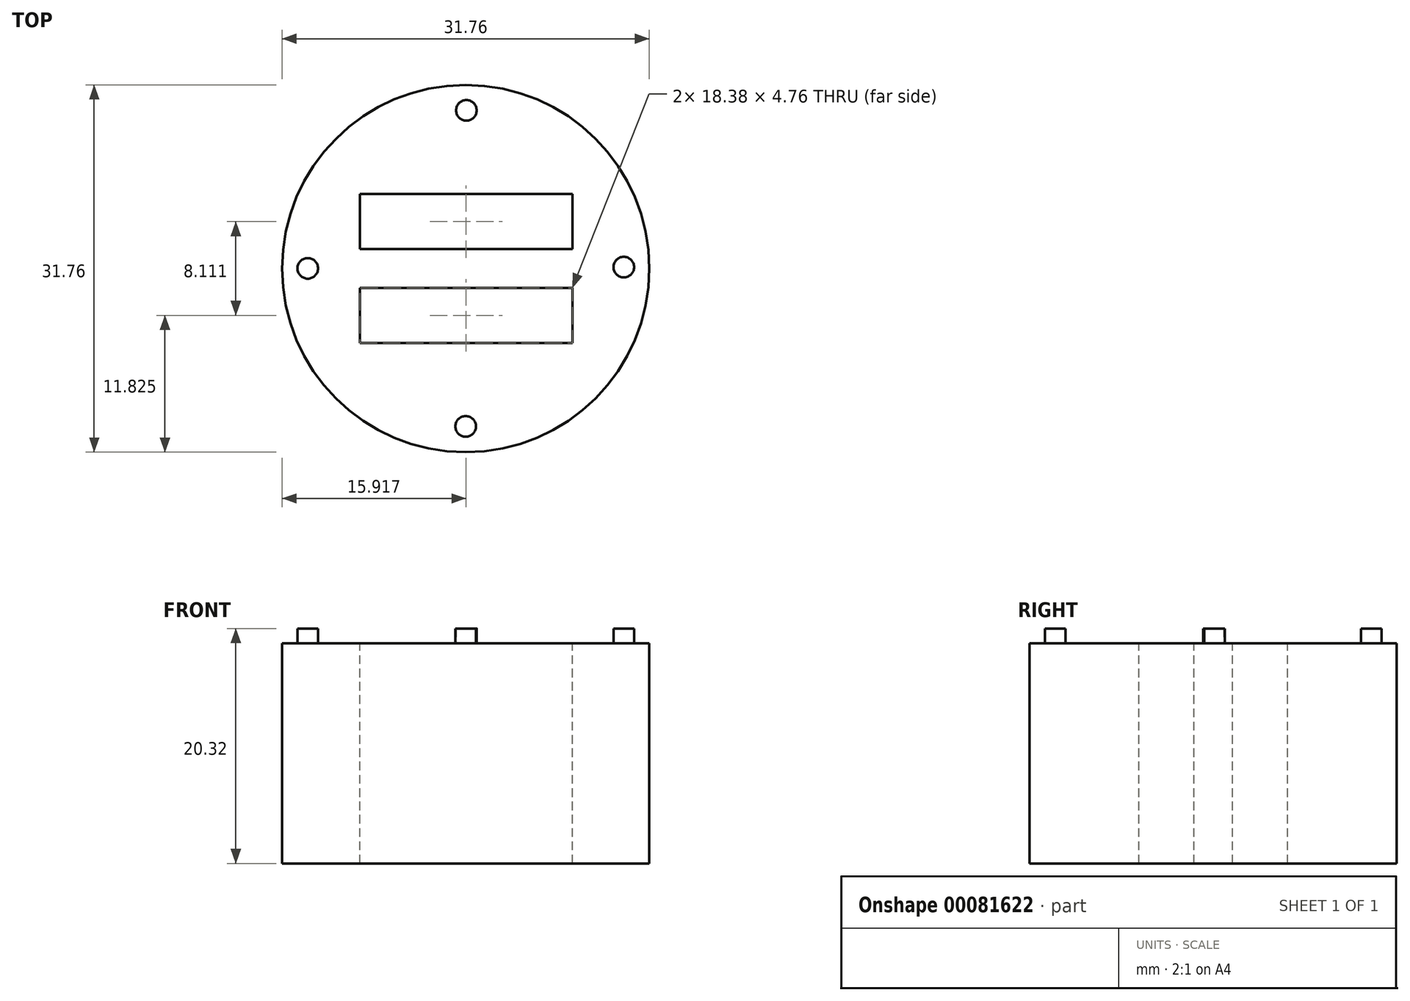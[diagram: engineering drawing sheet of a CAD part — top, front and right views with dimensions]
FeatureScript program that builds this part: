
annotation { "Feature Type Name" : "Feature", "Feature Type Description" : "" }
export const myFeature = defineFeature(function(context is Context, id is Id, definition is map)
    precondition{}
    {
        {
            var Q0;
            Q0=qCreatedBy(makeId("Top.planeOp"),FACE);
            var sketch = newSketch(context, id + "F0", { "sketchPlane" : qUnion([Q0])});
            skCircle(sketch, "E0", {"center": v(0, 0) * mm, "radius": 15.88 * mm});
            skSolve(sketch);
        }
        {
            var Q0;
            Q0=qSketchRegion(id+"F0",true);
            extrude(context, id + "F1", {"entities" : qUnion([Q0]), "depth" : 19.05 * mm});
        }
        {
            var Q0;
            Q0=makeQuery(id+"F1.opExtrude","CAP_FACE",FACE,{"disambiguationData":[OSD([sQuery(id+"F0.wireOp",EDGE,"E0")])],"isStart":true});
            var sketch = newSketch(context, id + "F2", { "sketchPlane" : qUnion([Q0])});
            skCircle(sketch, "E1", {"center": v(0, 0) * mm, "radius": 12.7 * mm});
            skSolve(sketch);
        }
        {
            var Q0;
            Q0=makeQuery(id+"F2.imprint","IMPRINT",FACE,{"disambiguationData":[TD([[makeQuery(id+"F2.imprint","IMPRINT",EDGE,{"derivedFrom":sQuery(id+"F2.wireOp",EDGE,"E1")}),-1.0]])]});
            var sketch = newSketch(context, id + "F3", { "sketchPlane" : qUnion([Q0])});
            skCircle(sketch, "E2", {"center": v(0, 13.65) * mm, "radius": 0.89 * mm});
            skCircle(sketch, "E3", {"center": v(-13.66, -0.02) * mm, "radius": 0.89 * mm});
            skCircle(sketch, "E4", {"center": v(0.06, -13.68) * mm, "radius": 0.89 * mm});
            skCircle(sketch, "E5", {"center": v(13.67, -0.12) * mm, "radius": 0.89 * mm});
            skSolve(sketch);
        }
        {
            var Q0;
            Q0=makeQuery(id+"F1.opExtrude","CAP_FACE",FACE,{"disambiguationData":[OSD([sQuery(id+"F0.wireOp",EDGE,"E0")])],"isStart":false});
            var sketch = newSketch(context, id + "F4", { "sketchPlane" : qUnion([Q0])});
            skLineSegment(sketch, "E6", {"start": v(0, 12.85) * mm, "end": v(0, -12.7) * mm});
            skLineSegment(sketch, "E7", {"start": v(0, -12.7) * mm, "end": v(-12.6, 0) * mm});
            skLineSegment(sketch, "E8", {"start": v(-12.6, 0) * mm, "end": v(0, 12.85) * mm});
            skLineSegment(sketch, "E9", {"start": v(0, 12.85) * mm, "end": v(12.68, 0) * mm});
            skLineSegment(sketch, "E10", {"start": v(12.68, 0) * mm, "end": v(0, -12.7) * mm});
            skLineSegment(sketch, "E11", {"start": v(-12.6, 0) * mm, "end": v(12.68, 0) * mm});
            skLineSegment(sketch, "E12", {"start": v(-6.3, -6.35) * mm, "end": v(9.08, 8.92) * mm});
            skLineSegment(sketch, "E13", {"start": v(-6.3, 6.43) * mm, "end": v(9.08, -9.08) * mm});
            skLineSegment(sketch, "E14", {"start": v(-6.3, -6.35) * mm, "end": v(-9.02, -9.05) * mm});
            skLineSegment(sketch, "E15", {"start": v(-6.3, 6.43) * mm, "end": v(-8.94, 9.08) * mm});
            skLineSegment(sketch, "E16", {"start": v(-8.94, 9.08) * mm, "end": v(-12.6, 0) * mm});
            skLineSegment(sketch, "E17", {"start": v(-12.6, 0) * mm, "end": v(-9.02, -9.05) * mm});
            skLineSegment(sketch, "E18", {"start": v(-9.02, -9.05) * mm, "end": v(0, -12.7) * mm});
            skLineSegment(sketch, "E19", {"start": v(0, -12.7) * mm, "end": v(9.08, -9.08) * mm});
            skLineSegment(sketch, "E20", {"start": v(9.08, -9.08) * mm, "end": v(12.68, 0) * mm});
            skLineSegment(sketch, "E21", {"start": v(12.68, 0) * mm, "end": v(9.08, 8.92) * mm});
            skLineSegment(sketch, "E22", {"start": v(9.08, 8.92) * mm, "end": v(0, 12.85) * mm});
            skLineSegment(sketch, "E23", {"start": v(0, 12.85) * mm, "end": v(-8.94, 9.08) * mm});
            skSolve(sketch);
        }
        {
            var Q0;
            Q0=makeQuery(id+"F1.opExtrude","CAP_FACE",FACE,{"disambiguationData":[OSD([sQuery(id+"F0.wireOp",EDGE,"E0")])],"isStart":false});
            var sketch = newSketch(context, id + "F5", { "sketchPlane" : qUnion([Q0])});
            skCircle(sketch, "E24", {"center": v(0, 0) * mm, "radius": 11.35 * mm});
            skSolve(sketch);
        }
        {
            var Q0;
            Q0=makeQuery(id+"F1.opExtrude","CAP_FACE",FACE,{"disambiguationData":[OSD([sQuery(id+"F0.wireOp",EDGE,"E0")])],"isStart":false});
            var sketch = newSketch(context, id + "F6", { "sketchPlane" : qUnion([Q0])});
            skLineSegment(sketch, "E25.bottom", {"start": v(-9.15, 1.67) * mm, "end": v(9.23, 1.67) * mm});
            skLineSegment(sketch, "E25.top", {"start": v(-9.15, 6.44) * mm, "end": v(9.23, 6.44) * mm});
            skLineSegment(sketch, "E25.left", {"start": v(-9.15, 1.67) * mm, "end": v(-9.15, 6.44) * mm});
            skLineSegment(sketch, "E25.right", {"start": v(9.23, 1.67) * mm, "end": v(9.23, 6.44) * mm});
            skLineSegment(sketch, "E26.MirrorCS", {"start": v(-9.15, -6.44) * mm, "end": v(9.23, -6.44) * mm});
            skLineSegment(sketch, "E27.MirrorCS", {"start": v(-9.15, -1.67) * mm, "end": v(9.23, -1.67) * mm});
            skLineSegment(sketch, "E28.MirrorCS", {"start": v(9.23, -1.67) * mm, "end": v(9.23, -6.44) * mm});
            skLineSegment(sketch, "E29.MirrorCS", {"start": v(-9.15, -1.67) * mm, "end": v(-9.15, -6.44) * mm});
            skSolve(sketch);
        }
        {
            var Q0;
            Q0 = qSketchRegion(id + "F6", true);
            extrude(context, id + "F7", {"entities" : qUnion([Q0]), "operationType" : NewBodyOperationType.REMOVE, "oppositeDirection" : true, "depth" : 19.05 * mm});
        }
        {
            var Q0;
            Q0 = qSketchRegion(id + "F3", true);
            extrude(context, id + "F8", {"entities" : qUnion([Q0]), "operationType" : NewBodyOperationType.ADD, "oppositeDirection" : true, "depth" : 20.32 * mm});
        }
    });
